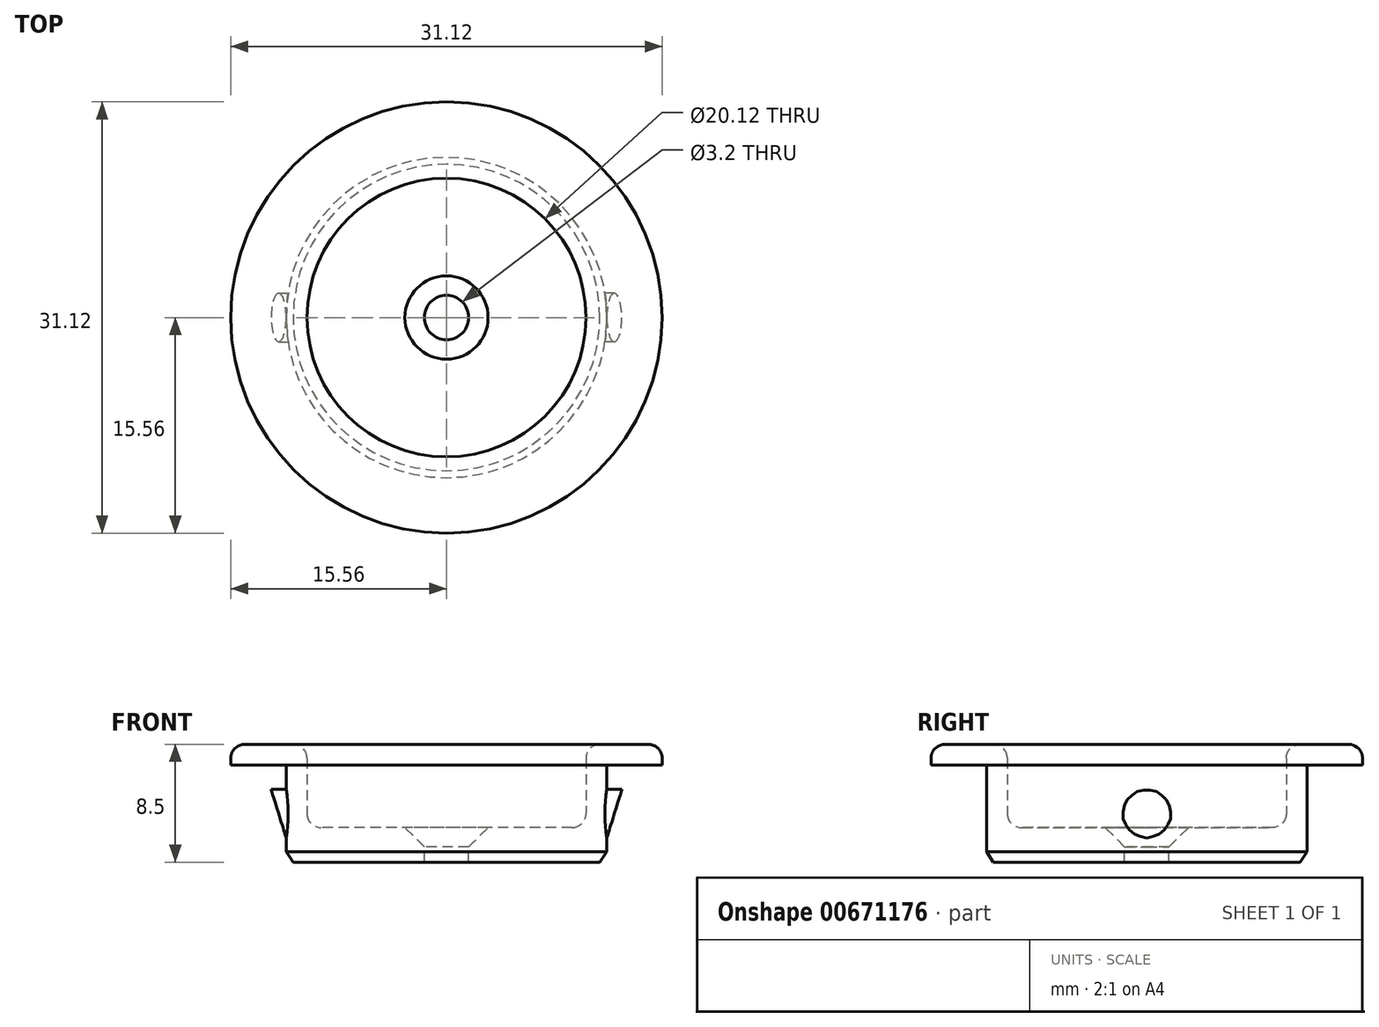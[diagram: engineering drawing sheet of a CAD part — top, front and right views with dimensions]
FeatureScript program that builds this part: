
annotation { "Feature Type Name" : "Feature", "Feature Type Description" : "" }
export const myFeature = defineFeature(function(context is Context, id is Id, definition is map)
    precondition{}
    {
        {
            var Q0;
            Q0=qCreatedBy(makeId("Front.planeOp"),FACE);
            var sketch = newSketch(context, id + "F0", { "sketchPlane" : qUnion([Q0])});
            skLineSegment(sketch, "E0", {"start": v(0, 0) * mm, "end": v(11.56, 0) * mm});
            skLineSegment(sketch, "E1", {"start": v(11.56, 0) * mm, "end": v(11.56, 7) * mm});
            skLineSegment(sketch, "E2", {"start": v(11.56, 7) * mm, "end": v(15.56, 7) * mm});
            skLineSegment(sketch, "E3", {"start": v(15.56, 7) * mm, "end": v(15.56, 8.5) * mm});
            skLineSegment(sketch, "E4", {"start": v(15.56, 8.5) * mm, "end": v(10.06, 8.5) * mm});
            skLineSegment(sketch, "E5", {"start": v(10.06, 8.5) * mm, "end": v(10.06, 2.5) * mm});
            skLineSegment(sketch, "E6", {"start": v(10.06, 2.5) * mm, "end": v(0, 2.5) * mm});
            skLineSegment(sketch, "E7", {"start": v(0, 2.5) * mm, "end": v(0, 0) * mm});
            skLineSegment(sketch, "E8", {"start": v(0, 9.77) * mm, "end": v(0, 36.51) * mm});
            skSolve(sketch);
        }
        {
            var Q0;
            Q0=makeQuery(id+"F0.imprint","IMPRINT",FACE,{"disambiguationData":[TD([[makeQuery(id+"F0.imprint","IMPRINT",EDGE,{"derivedFrom":sQuery(id+"F0.wireOp",EDGE,"E0")}),1.0]])]});
            var Q1;
            Q1=sQuery(id+"F0.wireOp",EDGE,"E8");
            revolve(context, id + "F1", {"entities" : qUnion([Q0]), "axis" : qUnion([Q1]), "revolveType" : RevolveType.FULL});
        }
        {
            var Q0;
            Q0=makeQuery(id+"F1.opRevolve","SWEPT_EDGE",EDGE,{"disambiguationData":[OSD([sQuery(id+"F0.wireOp",EDGE,"E3"),sQuery(id+"F0.wireOp",EDGE,"E4")])]});
            var Q1;
            Q1=makeQuery(id+"F1.opRevolve","SWEPT_EDGE",EDGE,{"disambiguationData":[OSD([sQuery(id+"F0.wireOp",EDGE,"E4"),sQuery(id+"F0.wireOp",EDGE,"E5")])]});
            var Q2;
            Q2=makeQuery(id+"F1.opRevolve","SWEPT_EDGE",EDGE,{"disambiguationData":[OSD([sQuery(id+"F0.wireOp",EDGE,"E5"),sQuery(id+"F0.wireOp",EDGE,"E6")])]});
            fillet(context, id + "F2", {"entities" : qUnion([Q0, Q1, Q2]), "radius" : 1 * mm, "tangentPropagation" : true, "allowEdgeOverflow" : false});
        }
        {
            var Q0;
            Q0=makeQuery(id+"F1.opRevolve","SWEPT_EDGE",EDGE,{"disambiguationData":[OSD([sQuery(id+"F0.wireOp",EDGE,"E0"),sQuery(id+"F0.wireOp",EDGE,"E1")])]});
            chamfer(context, id + "F3", {"entities" : qUnion([Q0]), "chamferType" : ChamferType.TWO_OFFSETS, "width1" : .5 * mm, "oppositeDirection" : false, "width2" : .75 * mm, "tangentPropagation" : true});
        }
        {
            var Q0;
            Q0=qCreatedBy(makeId("Right.planeOp"),FACE);
            cPlane(context, id + "F4", {"entities" : qUnion([Q0]), "cplaneType" : CPlaneType.OFFSET, "offset" : 11.4 * mm, "width" : 150 * mm, "height" : 150 * mm});
        }
        {
            var Q0;
            Q0=qCreatedBy(id+"F4.planeOp",FACE);
            var sketch = newSketch(context, id + "F5", { "sketchPlane" : qUnion([Q0])});
            skCircle(sketch, "E9", {"center": v(0, 3.5) * mm, "radius": 1.75 * mm});
            skSolve(sketch);
        }
        {
            var Q0;
            Q0 = qSketchRegion(id + "F5", true);
            extrude(context, id + "F6", {"entities" : qUnion([Q0]), "operationType" : NewBodyOperationType.ADD, "depth" : 1.25 * mm, "offsetDistance" : 25 * mm});
        }
        {
            var Q0;
            Q0=qCreatedBy(makeId("Right.planeOp"),FACE);
            cPlane(context, id + "F7", {"entities" : qUnion([Q0]), "cplaneType" : CPlaneType.OFFSET, "offset" : 11.4 * mm, "oppositeDirection" : true, "width" : 150 * mm, "height" : 150 * mm});
        }
        {
            var Q0;
            Q0=qCreatedBy(id+"F7.planeOp",FACE);
            var sketch = newSketch(context, id + "F8", { "sketchPlane" : qUnion([Q0])});
            skCircle(sketch, "E10", {"center": v(0, 3.5) * mm, "radius": 1.75 * mm});
            skSolve(sketch);
        }
        {
            var Q0;
            Q0 = qSketchRegion(id + "F8", true);
            extrude(context, id + "F9", {"entities" : qUnion([Q0]), "operationType" : NewBodyOperationType.ADD, "oppositeDirection" : true, "depth" : 1.25 * mm, "offsetDistance" : 25 * mm});
        }
        {
            var Q0;
            Q0=qCreatedBy(makeId("Front.planeOp"),FACE);
            var sketch = newSketch(context, id + "F10", { "sketchPlane" : qUnion([Q0])});
            skLineSegment(sketch, "E11", {"start": v(-11.56, 1.75) * mm, "end": v(-12.65, 5.25) * mm});
            skLineSegment(sketch, "E12", {"start": v(-12.65, 5.25) * mm, "end": v(-13, 5.25) * mm});
            skLineSegment(sketch, "E13", {"start": v(-13, 5.25) * mm, "end": v(-13, 1.75) * mm});
            skLineSegment(sketch, "E14", {"start": v(-13, 1.75) * mm, "end": v(-11.56, 1.75) * mm});
            skLineSegment(sketch, "E15", {"start": v(11.56, 1.75) * mm, "end": v(13, 1.75) * mm});
            skLineSegment(sketch, "E16", {"start": v(13, 1.75) * mm, "end": v(13, 5.25) * mm});
            skLineSegment(sketch, "E17", {"start": v(13, 5.25) * mm, "end": v(12.65, 5.25) * mm});
            skLineSegment(sketch, "E18", {"start": v(12.65, 5.25) * mm, "end": v(11.56, 1.75) * mm});
            skSolve(sketch);
        }
        {
            var Q0;
            Q0 = qSketchRegion(id + "F10", true);
            extrude(context, id + "F11", {"entities" : qUnion([Q0]), "operationType" : NewBodyOperationType.REMOVE, "oppositeDirection" : true, "depth" : 1.75 * mm, "offsetDistance" : 25 * mm});
        }
        {
            var Q0;
            Q0 = qSketchRegion(id + "F10", true);
            extrude(context, id + "F12", {"entities" : qUnion([Q0]), "operationType" : NewBodyOperationType.REMOVE, "depth" : 1.75 * mm, "offsetDistance" : 25 * mm});
        }
        {
            var Q0;
            Q0=makeQuery(id+"F1.opRevolve","SWEPT_FACE",FACE,{"disambiguationData":[OSD([sQuery(id+"F0.wireOp",EDGE,"E6")])]});
            var sketch = newSketch(context, id + "F13", { "sketchPlane" : qUnion([Q0])});
            skPoint(sketch, "E19", {"position": v(0, 0) * mm});
            skSolve(sketch);
        }
        {
            var Q0;
            Q0=sQuery(id+"F13.wireOp",VERTEX,"E19");
            var Q1;
            Q1=makeQuery(id+"F1.opRevolve","SWEPT_BODY",BODY,{"disambiguationData":[OSD([sQuery(id+"F0.wireOp",EDGE,"E0"),sQuery(id+"F0.wireOp",EDGE,"E1"),sQuery(id+"F0.wireOp",EDGE,"E2"),sQuery(id+"F0.wireOp",EDGE,"E3"),sQuery(id+"F0.wireOp",EDGE,"E4"),sQuery(id+"F0.wireOp",EDGE,"E5"),sQuery(id+"F0.wireOp",EDGE,"E6"),sQuery(id+"F0.wireOp",EDGE,"E7")])]});
            hole(context, id + "F14", {"style" : HoleStyle.C_SINK, "endStyle" : HoleEndStyle.BLIND, "holeDiameter" : 3.2 * mm, "cSinkDiameter" : 6 * mm, "cSinkAngle" : 90 * degree, "majorDiameter" : 5 * mm, "holeDepth" : 4.5 * mm, "isTappedThrough" : true, "tappedDepth" : 12 * mm, "tapClearance" : 3, "startFromSketch" : true, "locations" : qUnion([Q0]), "scope" : qUnion([Q1])});
        }
    });
